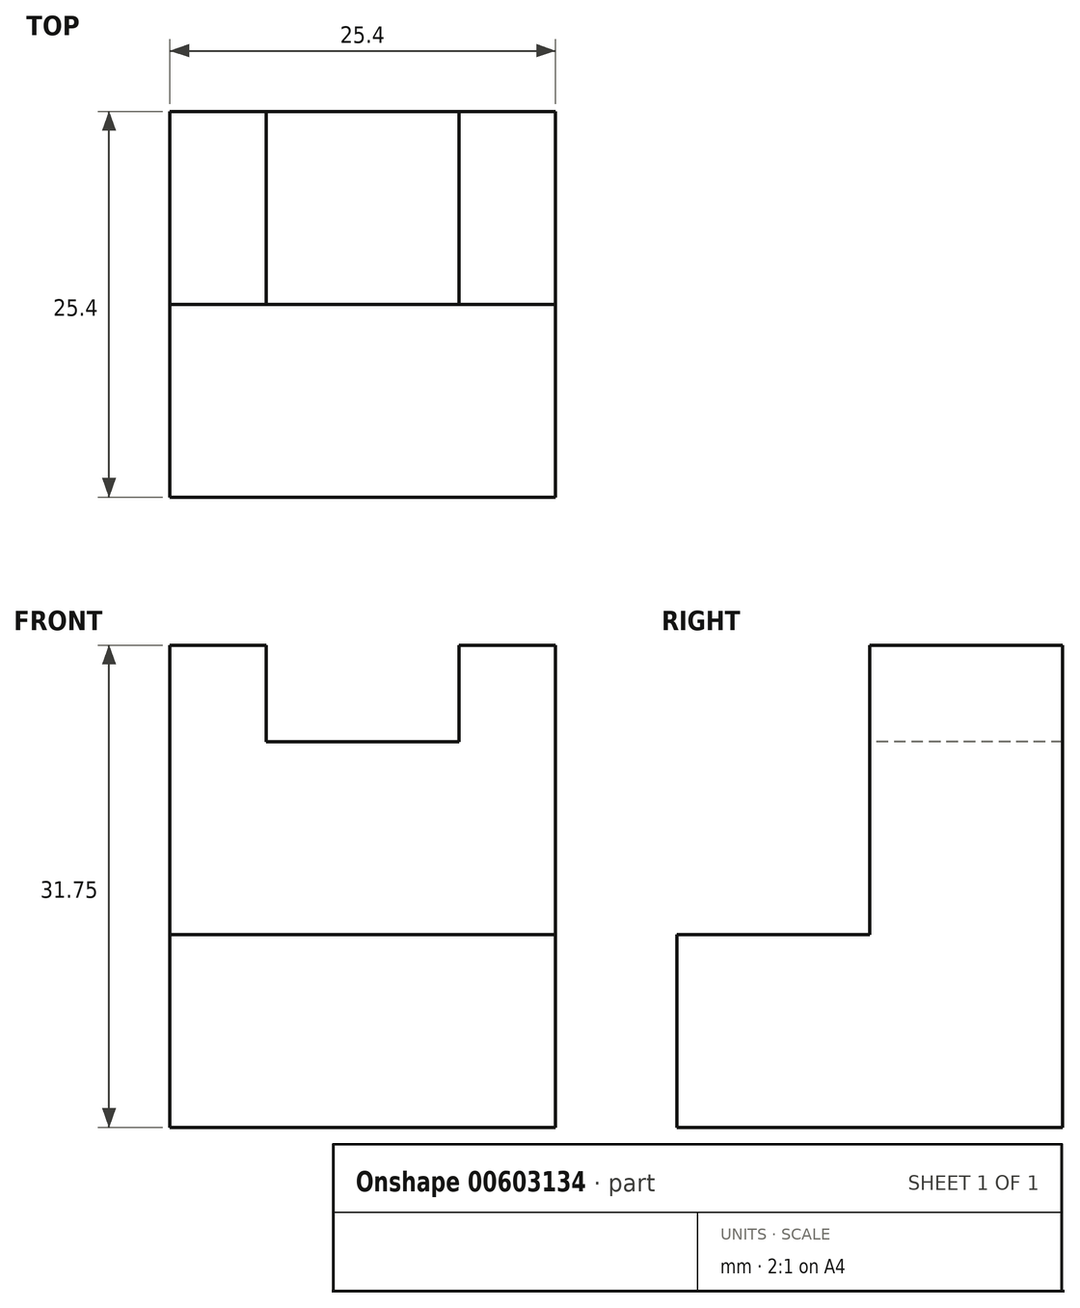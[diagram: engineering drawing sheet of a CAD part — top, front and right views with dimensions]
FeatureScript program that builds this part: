
annotation { "Feature Type Name" : "Feature", "Feature Type Description" : "" }
export const myFeature = defineFeature(function(context is Context, id is Id, definition is map)
    precondition{}
    {
        {
            var Q0;
            Q0=qCreatedBy(makeId("Right.planeOp"),FACE);
            var sketch = newSketch(context, id + "F0", { "sketchPlane" : qUnion([Q0])});
            skLineSegment(sketch, "E0", {"start": v(0, 0) * mm, "end": v(0, 31.75) * mm});
            skLineSegment(sketch, "E1", {"start": v(0, 31.75) * mm, "end": v(-12.7, 31.75) * mm});
            skLineSegment(sketch, "E2", {"start": v(-12.7, 31.75) * mm, "end": v(-12.7, 12.7) * mm});
            skLineSegment(sketch, "E3", {"start": v(-12.7, 12.7) * mm, "end": v(-25.4, 12.7) * mm});
            skLineSegment(sketch, "E4", {"start": v(-25.4, 12.7) * mm, "end": v(-25.4, 0) * mm});
            skLineSegment(sketch, "E5", {"start": v(-25.4, 0) * mm, "end": v(0, 0) * mm});
            skSolve(sketch);
        }
        {
            var Q0;
            Q0 = qSketchRegion(id + "F0", true);
            extrude(context, id + "F1", {"entities" : qUnion([Q0]), "depth" : 25.4 * mm, "offsetDistance" : 25.4 * mm});
        }
        {
            var Q0;
            Q0=makeQuery(id+"F1.opExtrude","SWEPT_FACE",FACE,{"disambiguationData":[OSD([sQuery(id+"F0.wireOp",EDGE,"E1")])]});
            var sketch = newSketch(context, id + "F2", { "sketchPlane" : qUnion([Q0])});
            skLineSegment(sketch, "E6", {"start": v(6.35, 0) * mm, "end": v(6.35, -12.7) * mm});
            skLineSegment(sketch, "E7", {"start": v(6.35, -12.7) * mm, "end": v(19.05, -12.7) * mm});
            skLineSegment(sketch, "E8", {"start": v(19.05, -12.7) * mm, "end": v(19.05, 0) * mm});
            skLineSegment(sketch, "E9", {"start": v(19.05, 0) * mm, "end": v(6.35, 0) * mm});
            skSolve(sketch);
        }
        {
            var Q0;
            Q0 = qSketchRegion(id + "F2", true);
            extrude(context, id + "F3", {"entities" : qUnion([Q0]), "operationType" : NewBodyOperationType.REMOVE, "oppositeDirection" : true, "depth" : 6.35 * mm, "offsetDistance" : 25.4 * mm});
        }
    });
